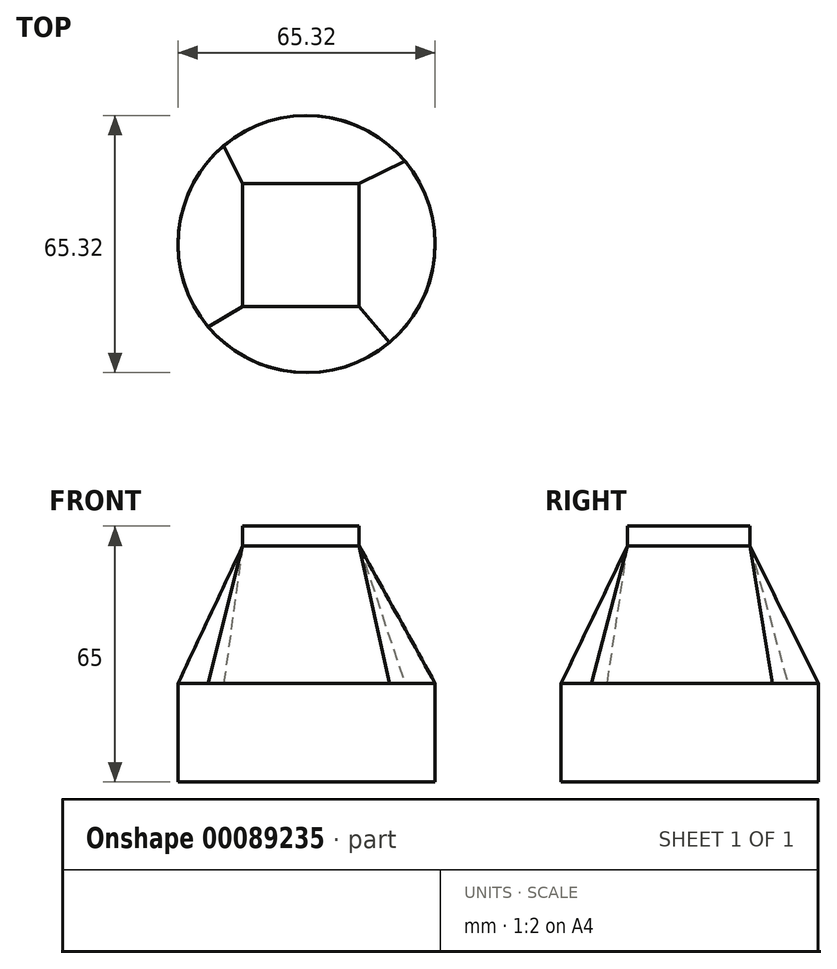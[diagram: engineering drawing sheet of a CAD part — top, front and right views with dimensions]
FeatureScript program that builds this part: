
annotation { "Feature Type Name" : "Feature", "Feature Type Description" : "" }
export const myFeature = defineFeature(function(context is Context, id is Id, definition is map)
    precondition{}
    {
        {
            var Q0;
            Q0=qCreatedBy(makeId("Top.planeOp"),FACE);
            var sketch = newSketch(context, id + "F0", { "sketchPlane" : qUnion([Q0])});
            skCircle(sketch, "E0", {"center": v(0, 0) * mm, "radius": 32.66 * mm});
            skSolve(sketch);
        }
        {
            var Q0;
            Q0=makeQuery(id+"F0.imprint","IMPRINT",FACE,{"disambiguationData":[TD([[makeQuery(id+"F0.imprint","IMPRINT",EDGE,{"derivedFrom":sQuery(id+"F0.wireOp",EDGE,"E0")}),1.0]])]});
            extrude(context, id + "F1", {"entities" : qUnion([Q0]), "depth" : 25 * mm});
        }
        {
            var Q0;
            Q0=qCreatedBy(makeId("Top.planeOp"),FACE);
            cPlane(context, id + "F2", {"entities" : qUnion([Q0]), "cplaneType" : CPlaneType.OFFSET, "offset" : 60 * mm, "width" : 150 * mm, "height" : 150 * mm});
        }
        {
            var Q0;
            Q0=qCreatedBy(id+"F2.planeOp",FACE);
            var sketch = newSketch(context, id + "F3", { "sketchPlane" : qUnion([Q0])});
            skLineSegment(sketch, "E1.bottom", {"start": v(13.37, -15.85) * mm, "end": v(-16.25, -15.85) * mm});
            skLineSegment(sketch, "E1.top", {"start": v(13.37, 15.33) * mm, "end": v(-16.25, 15.33) * mm});
            skLineSegment(sketch, "E1.left", {"start": v(13.37, -15.85) * mm, "end": v(13.37, 15.33) * mm});
            skLineSegment(sketch, "E1.right", {"start": v(-16.25, -15.85) * mm, "end": v(-16.25, 15.33) * mm});
            skLineSegment(sketch, "E2.bottom", {"start": v(36.16, -39.96) * mm, "end": v(-36.82, -39.96) * mm});
            skLineSegment(sketch, "E2.top", {"start": v(36.16, 34.75) * mm, "end": v(-36.82, 34.75) * mm});
            skLineSegment(sketch, "E2.left", {"start": v(36.16, -39.96) * mm, "end": v(36.16, 34.75) * mm});
            skLineSegment(sketch, "E2.right", {"start": v(-36.82, -39.96) * mm, "end": v(-36.82, 34.75) * mm});
            skSolve(sketch);
        }
        {
            var Q0;
            Q0=makeQuery(id+"F3.imprint","IMPRINT",FACE,{"disambiguationData":[TD([[makeQuery(id+"F3.imprint","IMPRINT",EDGE,{"derivedFrom":sQuery(id+"F3.wireOp",EDGE,"E1.bottom")}),-1.0]])]});
            extrude(context, id + "F4", {"entities" : qUnion([Q0]), "depth" : 5 * mm});
        }
        {
            var Q0;
            Q0=makeQuery(id+"F4.opExtrude","CAP_FACE",FACE,{"disambiguationData":[OSD([sQuery(id+"F3.wireOp",EDGE,"E1.bottom"),sQuery(id+"F3.wireOp",EDGE,"E1.top"),sQuery(id+"F3.wireOp",EDGE,"E1.left"),sQuery(id+"F3.wireOp",EDGE,"E1.right"),sQuery(id+"F3.wireOp",EDGE,"E2.bottom"),sQuery(id+"F3.wireOp",EDGE,"E2.top"),sQuery(id+"F3.wireOp",EDGE,"E2.left"),sQuery(id+"F3.wireOp",EDGE,"E2.right")])],"isStart":true});
            var Q1;
            Q1=makeQuery(id+"F1.opExtrude","CAP_FACE",FACE,{"disambiguationData":[OSD([sQuery(id+"F0.wireOp",EDGE,"E0"),sQuery(id+"F0.wireOp",EDGE,"T44F85nC-1GIT-a53I-S418-FGNwan0oAJ7z")])],"isStart":false});
            loft(context, id + "F5", {"sheetProfilesArray" : [{ "sheetProfileEntities" : qUnion([Q0]) }, { "sheetProfileEntities" : qUnion([Q1]) }]});
        }
    });
